# Revit family: Mixer-Kitchen-MA-Mora_Cera_245030
name_source: partatom
category: Plumbing Fixtures
revit_build: Autodesk Revit 2015 (Build: 20140606_1530(x64)
units: mm (PartAtom-declared; Revit-internal decimal feet)

## types (1)
- Flat end Ø10 mm, with low spout, dishwasher valve
    Article Number = 245030
    Assembly Code = D2010
    BIMobject category = Taps & Mixers
    Brand url = http://www.moraarmatur.se
    Care Instruction URL = http://www.moraarmatur.se
    Code EAN = 7391887233876
    Code LVI FIN = 6261201
    Code NRF NOR = -
    Code RSK SWE = 8318202
    Code VVS DNK = -
    Cold Water Connection Diameter = 10 mm  [stored 0.0328084 ft]
    Cold Water Connection Radius = 5 mm  [stored 0.0164042 ft]
    Connector Description = Flat end Ø10 mm / G1/2" DW-connector
    Description = Mora Cera K2 Kitchen Mixer low spout with dishwasher valve
    Design country = Sweden
    Dishwasher Connection Diameter = 19 mm  [stored 0.062336 ft]
    Dishwasher Connection Radius = 10 mm  [stored 0.0328084 ft]
    EAN code = https://7391887233876
    Edition number = 1
    Height = 157 mm
    Hot Water Connection Diameter = 10 mm  [stored 0.0328084 ft]
    Hot Water Connection Radius = 5 mm  [stored 0.0164042 ft]
    IFC Classification = Furnishing Element
    Installation Instruction URL = http://www.moraarmatur.se
    Installation instructions = http://www.moraarmatur.se
    Length = 218 mm
    Manufacturer = Mora Armatur
    Manufacturer country = Sweden
    Manufacturer name = Mora Armatur
    Masterformat 2014 Code = 22 41 39
    Masterformat 2014 Description = Residential Faucets, Supplies, and Trim
    Material = Mora Armatur Chrome - Polished
    Material main = Brass
    Material secondary = Chrome
    Model = 245030
    NBS Reference Code = 35-79-79
    NBS Reference Description = Sink Water Supply Fittings
    Nominal Flow = 0.0 L/s
    Nominal height = 0 mm  [stored 0 ft]
    Nominal width = 0 mm  [stored 0 ft]
    OmniClass Code = 23-31 11 00
    OmniClass Description = Faucets
    Pressure Drop = 0.0 kPa
    Product Guid = ba279349-4174-4976-a0ab-06681f67ee15
    Product Page URL = http://www.moraarmatur.se
    Product SKU = 245030
    Product certification = http://www.moraarmatur.se
    Product data url = http://bimobject.com
    Product family = Kitchen Mixers
    Product group = Mora Cera
    Product url = http://www.moraarmatur.se
    QR code = http://bimobject.com
    Technical description = http://www.moraarmatur.se
    Type Comments = Flat end Ø10 mm, With low spout, dishwasher valve, Chrome
    UNSPSC Code = 3018
    URL = http://www.morararmatur.com
    Uniclass 1.4 Code = L725111
    Uniclass 1.4 Description = Mixer taps
    Uniclass 2.0 Code = PR-35-79-79
    Uniclass 2.0 Description = Sink Water Supply Fittings
    Uniclass 2015 Code = Pr_40_20_87_84
    Uniclass 2015 Name = Sink taps
    Uniformat II Code = D2010
    Uniformat II Description = Plumbing Fixtures
    Waste Connection = No
    Weight Net (Kg) = 0
    Youtube clip = http://www.moraarmatur.se

note: [stored X ft] marks values corroborated as IEEE doubles in the binary element streams (Revit-internal decimal feet)

## geometry (parser evidence)
native form markers: Blend x4, Sweep x3
no freeform markers — native parametric forms only
